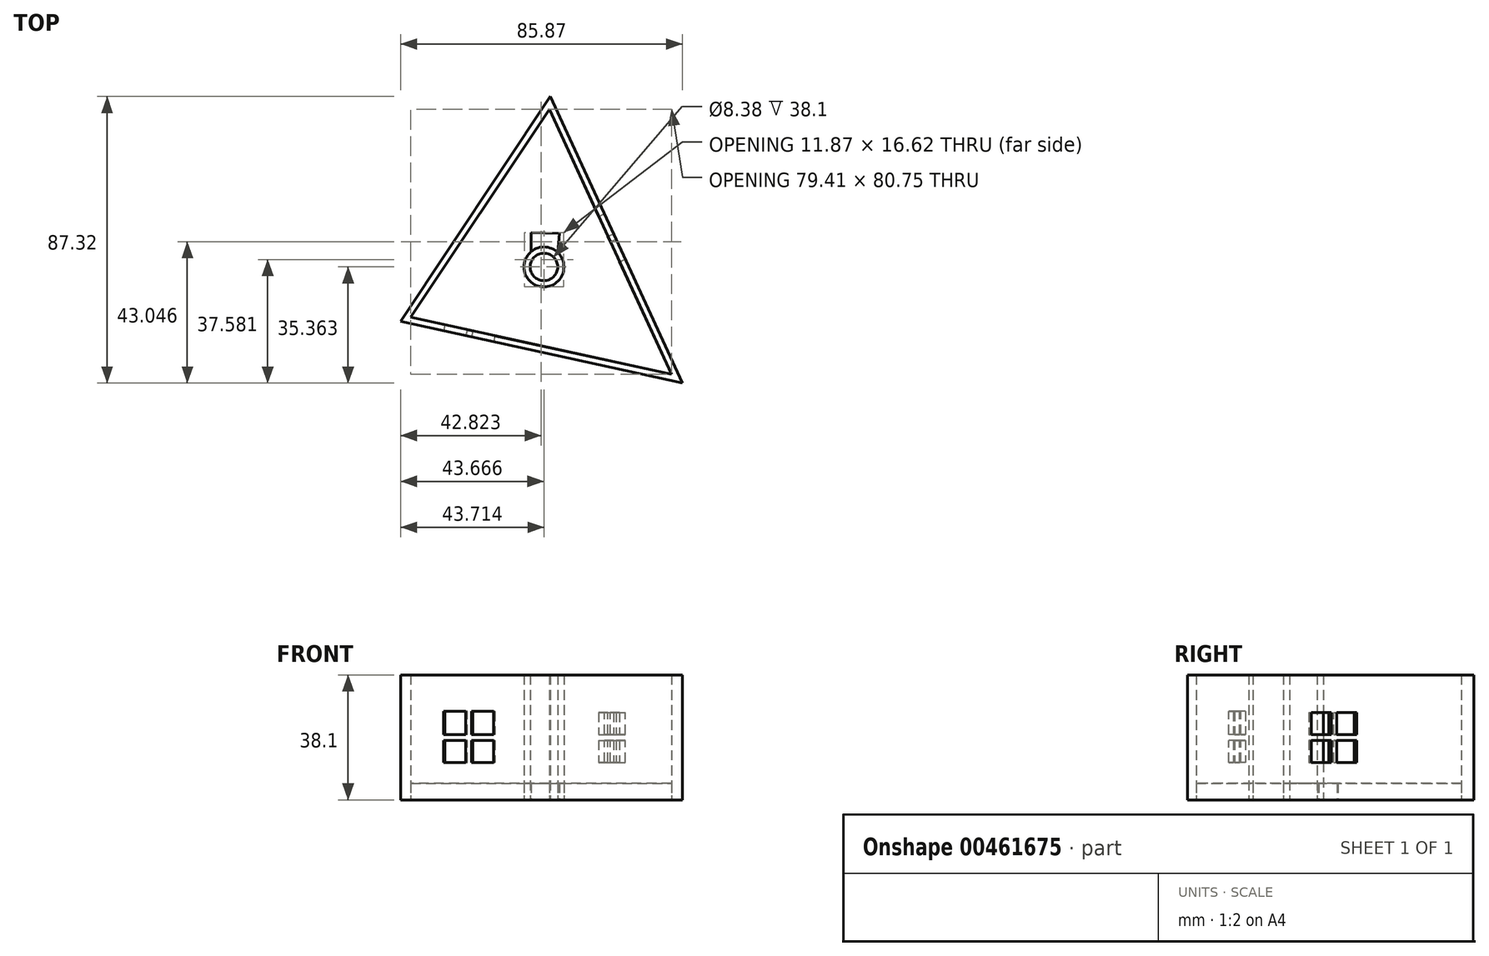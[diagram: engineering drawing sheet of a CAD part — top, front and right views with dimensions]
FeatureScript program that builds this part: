
annotation { "Feature Type Name" : "Feature", "Feature Type Description" : "" }
export const myFeature = defineFeature(function(context is Context, id is Id, definition is map)
    precondition{}
    {
        {
            var Q0;
            Q0=qCreatedBy(makeId("Top.planeOp"),FACE);
            var sketch = newSketch(context, id + "F0", { "sketchPlane" : qUnion([Q0])});
            skLineSegment(sketch, "E0", {"start": v(0, 47.93) * mm, "end": v(-42.23, -15.5) * mm});
            skLineSegment(sketch, "E1", {"start": v(-42.23, -15.5) * mm, "end": v(37.18, -32.82) * mm});
            skLineSegment(sketch, "E2", {"start": v(37.18, -32.82) * mm, "end": v(0, 47.93) * mm});
            skLineSegment(sketch, "E3", {"start": v(-2.53, -24.16) * mm, "end": v(0, 47.93) * mm, "construction": true});
            skLineSegment(sketch, "E4", {"start": v(18.59, 7.56) * mm, "end": v(-42.23, -15.5) * mm, "construction": true});
            skCircle(sketch, "E5", {"center": v(-1.68, -0.13) * mm, "radius": 4.19 * mm});
            skCircle(sketch, "E6", {"center": v(-1.68, -0.13) * mm, "radius": 6.1 * mm});
            skLineSegment(sketch, "E7", {"start": v(-21.12, 16.22) * mm, "end": v(37.18, -32.82) * mm, "construction": true});
            skLineSegment(sketch, "E8", {"start": v(-43.81, -14.44) * mm, "end": v(0.31, 51.83) * mm});
            skLineSegment(sketch, "E9", {"start": v(1.74, 48.73) * mm, "end": v(40.52, -35.49) * mm});
            skLineSegment(sketch, "E10", {"start": v(36.78, -34.67) * mm, "end": v(-45.35, -16.75) * mm});
            skLineSegment(sketch, "E11", {"start": v(-43.81, -14.44) * mm, "end": v(-45.35, -16.75) * mm});
            skLineSegment(sketch, "E12", {"start": v(36.78, -34.67) * mm, "end": v(40.52, -35.49) * mm});
            skLineSegment(sketch, "E13", {"start": v(1.74, 48.73) * mm, "end": v(0.31, 51.83) * mm});
            skLineSegment(sketch, "E14", {"start": v(-5.65, 10.4) * mm, "end": v(-1.32, 10.25) * mm});
            skLineSegment(sketch, "E15.MirrorCS", {"start": v(3.01, 10.1) * mm, "end": v(-1.32, 10.25) * mm});
            skLineSegment(sketch, "E16", {"start": v(-5.65, 10.4) * mm, "end": v(-5.65, 4.5) * mm});
            skLineSegment(sketch, "E17.MirrorCS", {"start": v(3.01, 10.1) * mm, "end": v(2.6, 4.2) * mm});
            skSolve(sketch);
        }
        {
            var Q0;
            Q0=makeQuery(id+"F0.imprint","IMPRINT",FACE,{"disambiguationData":[TD([[makeQuery(id+"F0.imprint","IMPRINT",EDGE,{"derivedFrom":sQuery(id+"F0.wireOp",EDGE,"E0")}),-1.0]])]});
            var Q1;
            Q1=makeQuery(id+"F0.imprint","IMPRINT",FACE,{"disambiguationData":[TD([[makeQuery(id+"F0.imprint","IMPRINT",EDGE,{"derivedFrom":sQuery(id+"F0.wireOp",EDGE,"E5")}),-1.0]])]});
            extrude(context, id + "F1", {"entities" : qUnion([Q0, Q1]), "depth" : 38.1 * mm});
        }
        {
            var Q0;
            Q0=makeQuery(id+"F0.imprint","IMPRINT",FACE,{"disambiguationData":[TD([[makeQuery(id+"F0.imprint","IMPRINT",EDGE,{"derivedFrom":sQuery(id+"F0.wireOp",EDGE,"E0")}),1.0]])]});
            extrude(context, id + "F2", {"entities" : qUnion([Q0]), "depth" : 5.08 * mm});
        }
        {
            var Q0;
            Q0=makeQuery(id+"F1.opExtrude","SWEPT_FACE",FACE,{"disambiguationData":[OSD([sQuery(id+"F0.wireOp",EDGE,"E10"),sQuery(id+"F0.wireOp",EDGE,"E12")])]});
            var sketch = newSketch(context, id + "F3", { "sketchPlane" : qUnion([Q0])});
            skLineSegment(sketch, "E18", {"start": v(3.2, 38.1) * mm, "end": v(3.2, 0) * mm, "construction": true});
            skLineSegment(sketch, "E19", {"start": v(-40.74, 19.05) * mm, "end": v(47.15, 19.05) * mm, "construction": true});
            skLineSegment(sketch, "E20", {"start": v(-19.5, 38.36) * mm, "end": v(-19.5, 0) * mm, "construction": true});
            skLineSegment(sketch, "E21.bottom", {"start": v(-11.7, 11.38) * mm, "end": v(-27.3, 11.38) * mm});
            skLineSegment(sketch, "E21.top", {"start": v(-11.7, 26.98) * mm, "end": v(-27.3, 26.98) * mm});
            skLineSegment(sketch, "E21.left", {"start": v(-11.7, 11.38) * mm, "end": v(-11.7, 26.98) * mm});
            skLineSegment(sketch, "E21.right", {"start": v(-27.3, 11.38) * mm, "end": v(-27.3, 26.98) * mm});
            skPoint(sketch, "E21.middle", {"position": v(-19.5, 19.18) * mm});
            skLineSegment(sketch, "E22", {"start": v(-20.4, 26.98) * mm, "end": v(-20.4, 11.38) * mm});
            skLineSegment(sketch, "E23.MirrorCS", {"start": v(-18.61, 26.98) * mm, "end": v(-18.61, 11.38) * mm});
            skLineSegment(sketch, "E24", {"start": v(-20.4, 26.98) * mm, "end": v(-18.61, 26.98) * mm});
            skLineSegment(sketch, "E25", {"start": v(-27.3, 18.16) * mm, "end": v(-11.7, 18.16) * mm});
            skLineSegment(sketch, "E26.MirrorCS", {"start": v(-27.3, 19.94) * mm, "end": v(-11.7, 19.94) * mm});
            skLineSegment(sketch, "E27", {"start": v(-27.3, 19.94) * mm, "end": v(-27.3, 18.16) * mm});
            skLineSegment(sketch, "E28.MirrorCS", {"start": v(18.12, 26.98) * mm, "end": v(33.71, 26.98) * mm});
            skLineSegment(sketch, "E29.MirrorCS", {"start": v(18.12, 11.38) * mm, "end": v(18.12, 26.98) * mm});
            skLineSegment(sketch, "E30.MirrorCS", {"start": v(33.71, 11.38) * mm, "end": v(33.71, 26.98) * mm});
            skLineSegment(sketch, "E31.MirrorCS", {"start": v(18.12, 11.38) * mm, "end": v(33.71, 11.38) * mm});
            skLineSegment(sketch, "E32.MirrorCS", {"start": v(33.71, 18.16) * mm, "end": v(18.12, 18.16) * mm});
            skLineSegment(sketch, "E33.MirrorCS", {"start": v(33.71, 19.94) * mm, "end": v(18.12, 19.94) * mm});
            skLineSegment(sketch, "E34.MirrorCS", {"start": v(26.8, 26.98) * mm, "end": v(26.8, 11.38) * mm});
            skLineSegment(sketch, "E35.MirrorCS", {"start": v(25.03, 26.98) * mm, "end": v(25.03, 11.38) * mm});
            skSolve(sketch);
        }
        {
            var Q0;
            {var subQ0=sQuery(id+"F3.wireOp",EDGE,"E21.right");var subQ1=sQuery(id+"F3.wireOp",EDGE,"E21.top");var subQ2=makeQuery(id+"F3.imprint","INTERSECT",VERTEX,{"derivedFrom":[subQ1,subQ0]});Q0=makeQuery(id+"F3.imprint","IMPRINT",FACE,{"disambiguationData":[TD([[makeQuery(id+"F3.imprint","IMPRINT",EDGE,{"disambiguationData":[TD([[subQ2,1.0]])],"derivedFrom":subQ1}),1.0]])]});}
            var Q1;
            {var subQ0=sQuery(id+"F3.wireOp",EDGE,"E21.right");var subQ1=sQuery(id+"F3.wireOp",EDGE,"E21.bottom");var subQ2=makeQuery(id+"F3.imprint","INTERSECT",VERTEX,{"derivedFrom":[subQ1,subQ0]});Q1=makeQuery(id+"F3.imprint","IMPRINT",FACE,{"disambiguationData":[TD([[makeQuery(id+"F3.imprint","IMPRINT",EDGE,{"disambiguationData":[TD([[subQ2,1.0]])],"derivedFrom":subQ1}),-1.0]])]});}
            var Q2;
            {var subQ0=sQuery(id+"F3.wireOp",EDGE,"E21.left");var subQ1=sQuery(id+"F3.wireOp",EDGE,"E21.bottom");var subQ2=makeQuery(id+"F3.imprint","INTERSECT",VERTEX,{"derivedFrom":[subQ1,subQ0]});Q2=makeQuery(id+"F3.imprint","IMPRINT",FACE,{"disambiguationData":[TD([[makeQuery(id+"F3.imprint","IMPRINT",EDGE,{"disambiguationData":[TD([[subQ2,-1.0]])],"derivedFrom":subQ1}),-1.0]])]});}
            var Q3;
            {var subQ0=sQuery(id+"F3.wireOp",EDGE,"E21.left");var subQ1=sQuery(id+"F3.wireOp",EDGE,"E21.top");var subQ2=makeQuery(id+"F3.imprint","INTERSECT",VERTEX,{"derivedFrom":[subQ1,subQ0]});Q3=makeQuery(id+"F3.imprint","IMPRINT",FACE,{"disambiguationData":[TD([[makeQuery(id+"F3.imprint","IMPRINT",EDGE,{"disambiguationData":[TD([[subQ2,1.0]])],"derivedFrom":subQ0}),1.0]])]});}
            extrude(context, id + "F4", {"entities" : qUnion([Q0, Q1, Q2, Q3]), "operationType" : NewBodyOperationType.REMOVE, "oppositeDirection" : true, "depth" : 1.9 * mm});
        }
        {
            var Q0;
            Q0=makeQuery(id+"F1.opExtrude","SWEPT_FACE",FACE,{"disambiguationData":[OSD([sQuery(id+"F0.wireOp",EDGE,"E9"),sQuery(id+"F0.wireOp",EDGE,"E13")])]});
            var sketch = newSketch(context, id + "F5", { "sketchPlane" : qUnion([Q0])});
            skLineSegment(sketch, "E36", {"start": v(0, 38.1) * mm, "end": v(0, 0) * mm, "construction": true});
            skPoint(sketch, "E36.startSnap0", {"position": v(-1.12, 38.1) * mm});
            skLineSegment(sketch, "E37", {"start": v(-49.18, 19.05) * mm, "end": v(46.95, 19.05) * mm, "construction": true});
            skLineSegment(sketch, "E38.bottom", {"start": v(7.62, 11.43) * mm, "end": v(-7.62, 11.43) * mm});
            skLineSegment(sketch, "E38.top", {"start": v(7.62, 26.67) * mm, "end": v(-7.62, 26.67) * mm});
            skLineSegment(sketch, "E38.left", {"start": v(7.62, 11.43) * mm, "end": v(7.62, 26.67) * mm});
            skLineSegment(sketch, "E38.right", {"start": v(-7.62, 11.43) * mm, "end": v(-7.62, 26.67) * mm});
            skPoint(sketch, "E38.middle", {"position": v(0, 19.05) * mm});
            skLineSegment(sketch, "E39", {"start": v(-0.89, 26.67) * mm, "end": v(-0.89, 11.43) * mm});
            skLineSegment(sketch, "E40", {"start": v(-7.62, 19.94) * mm, "end": v(7.62, 19.94) * mm});
            skLineSegment(sketch, "E41.MirrorCS", {"start": v(0.89, 26.67) * mm, "end": v(0.89, 11.43) * mm});
            skLineSegment(sketch, "E42.MirrorCS", {"start": v(-7.62, 18.16) * mm, "end": v(7.62, 18.16) * mm});
            skSolve(sketch);
        }
        {
            var Q0;
            {var subQ0=sQuery(id+"F5.wireOp",EDGE,"E38.right");var subQ1=sQuery(id+"F5.wireOp",EDGE,"E38.top");var subQ2=makeQuery(id+"F5.imprint","INTERSECT",VERTEX,{"derivedFrom":[subQ1,subQ0]});Q0=makeQuery(id+"F5.imprint","IMPRINT",FACE,{"disambiguationData":[TD([[makeQuery(id+"F5.imprint","IMPRINT",EDGE,{"disambiguationData":[TD([[subQ2,1.0]])],"derivedFrom":subQ1}),1.0]])]});}
            var Q1;
            {var subQ0=sQuery(id+"F5.wireOp",EDGE,"E38.right");var subQ1=sQuery(id+"F5.wireOp",EDGE,"E38.bottom");var subQ2=makeQuery(id+"F5.imprint","INTERSECT",VERTEX,{"derivedFrom":[subQ1,subQ0]});Q1=makeQuery(id+"F5.imprint","IMPRINT",FACE,{"disambiguationData":[TD([[makeQuery(id+"F5.imprint","IMPRINT",EDGE,{"disambiguationData":[TD([[subQ2,1.0]])],"derivedFrom":subQ1}),-1.0]])]});}
            var Q2;
            {var subQ0=sQuery(id+"F5.wireOp",EDGE,"E38.left");var subQ1=sQuery(id+"F5.wireOp",EDGE,"E38.bottom");var subQ2=makeQuery(id+"F5.imprint","INTERSECT",VERTEX,{"derivedFrom":[subQ1,subQ0]});Q2=makeQuery(id+"F5.imprint","IMPRINT",FACE,{"disambiguationData":[TD([[makeQuery(id+"F5.imprint","IMPRINT",EDGE,{"disambiguationData":[TD([[subQ2,-1.0]])],"derivedFrom":subQ1}),-1.0]])]});}
            var Q3;
            {var subQ0=sQuery(id+"F5.wireOp",EDGE,"E38.left");var subQ1=sQuery(id+"F5.wireOp",EDGE,"E38.top");var subQ2=makeQuery(id+"F5.imprint","INTERSECT",VERTEX,{"derivedFrom":[subQ1,subQ0]});Q3=makeQuery(id+"F5.imprint","IMPRINT",FACE,{"disambiguationData":[TD([[makeQuery(id+"F5.imprint","IMPRINT",EDGE,{"disambiguationData":[TD([[subQ2,-1.0]])],"derivedFrom":subQ1}),1.0]])]});}
            extrude(context, id + "F6", {"entities" : qUnion([Q0, Q1, Q2, Q3]), "operationType" : NewBodyOperationType.REMOVE, "oppositeDirection" : true, "depth" : 2.54 * mm});
        }
    });
